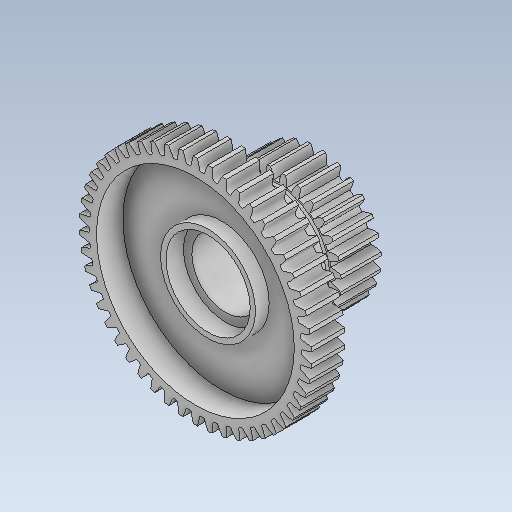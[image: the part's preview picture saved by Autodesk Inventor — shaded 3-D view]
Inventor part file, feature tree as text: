
AUTODESK INVENTOR PART (.ipt)
format: ipt  version: 2021 (Build 250183000, 183)  size: 629,248 bytes
history: native  units: in
note: dims shown in document units (in); Inventor stores cm internally (conversion verified against a paired STEP export)
features: chamfer x1
ambient origin geometry x8: Origin, YZ Plane, XZ Plane, XY Plane, X Axis, Y Axis, Z Axis, Center Point
bodies: Solid1 (feature_tree)
feature tree (1):
  chamfer  "Chamfer2"  [1 undecoded]
note: 1 required parameter value undecoded (feature->parameter linkage not recoverable at this tier; creation-order binding heuristic only, values carry confidence <= 0.55)
